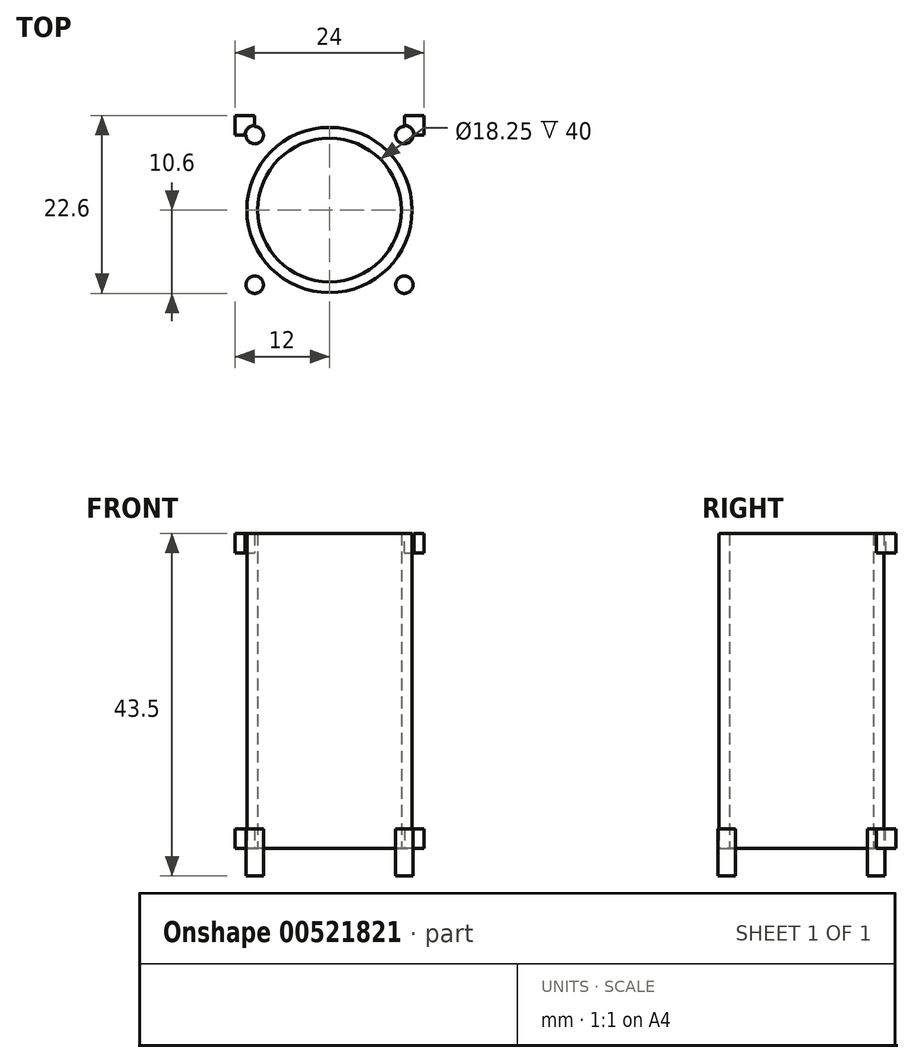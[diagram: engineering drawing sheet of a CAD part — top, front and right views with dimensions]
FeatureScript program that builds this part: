
annotation { "Feature Type Name" : "Feature", "Feature Type Description" : "" }
export const myFeature = defineFeature(function(context is Context, id is Id, definition is map)
    precondition{}
    {
        {
            var Q0;
            Q0=qCreatedBy(makeId("Top.planeOp"),FACE);
            var sketch = newSketch(context, id + "F0", { "sketchPlane" : qUnion([Q0])});
            skLineSegment(sketch, "E0.bottom", {"start": v(12, 12) * mm, "end": v(-12, 12) * mm});
            skLineSegment(sketch, "E0.top", {"start": v(12, -12) * mm, "end": v(-12, -12) * mm});
            skLineSegment(sketch, "E0.left", {"start": v(12, 12) * mm, "end": v(12, -12) * mm});
            skLineSegment(sketch, "E0.right", {"start": v(-12, 12) * mm, "end": v(-12, -12) * mm});
            skPoint(sketch, "E0.middle", {"position": v(0, 0) * mm});
            skLineSegment(sketch, "E1.bottom", {"start": v(-12, 12) * mm, "end": v(-9.5, 12) * mm});
            skLineSegment(sketch, "E1.top", {"start": v(-12, 9.5) * mm, "end": v(-9.5, 9.5) * mm});
            skLineSegment(sketch, "E1.left", {"start": v(-12, 12) * mm, "end": v(-12, 9.5) * mm});
            skLineSegment(sketch, "E1.right", {"start": v(-9.5, 12) * mm, "end": v(-9.5, 9.5) * mm});
            skLineSegment(sketch, "E2.bottom", {"start": v(12, 12) * mm, "end": v(9.5, 12) * mm});
            skLineSegment(sketch, "E2.top", {"start": v(12, 9.5) * mm, "end": v(9.5, 9.5) * mm});
            skLineSegment(sketch, "E2.left", {"start": v(12, 12) * mm, "end": v(12, 9.5) * mm});
            skLineSegment(sketch, "E2.right", {"start": v(9.5, 12) * mm, "end": v(9.5, 9.5) * mm});
            skLineSegment(sketch, "E3.bottom", {"start": v(12, -12) * mm, "end": v(9.5, -12) * mm});
            skLineSegment(sketch, "E3.top", {"start": v(12, -9.5) * mm, "end": v(9.5, -9.5) * mm});
            skLineSegment(sketch, "E3.left", {"start": v(12, -12) * mm, "end": v(12, -9.5) * mm});
            skLineSegment(sketch, "E3.right", {"start": v(9.5, -12) * mm, "end": v(9.5, -9.5) * mm});
            skLineSegment(sketch, "E4.bottom", {"start": v(-12, -12) * mm, "end": v(-9.5, -12) * mm});
            skLineSegment(sketch, "E4.top", {"start": v(-12, -9.5) * mm, "end": v(-9.5, -9.5) * mm});
            skLineSegment(sketch, "E4.left", {"start": v(-12, -12) * mm, "end": v(-12, -9.5) * mm});
            skLineSegment(sketch, "E4.right", {"start": v(-9.5, -12) * mm, "end": v(-9.5, -9.5) * mm});
            skCircle(sketch, "E5", {"center": v(0, 0) * mm, "radius": 9.12 * mm});
            skCircle(sketch, "E6", {"center": v(0, 0) * mm, "radius": 10.5 * mm});
            skCircle(sketch, "E7", {"center": v(9.5, 9.5) * mm, "radius": 1.1 * mm});
            skCircle(sketch, "E8", {"center": v(9.5, -9.5) * mm, "radius": 1.1 * mm});
            skCircle(sketch, "E9", {"center": v(-9.5, -9.5) * mm, "radius": 1.1 * mm});
            skCircle(sketch, "E10", {"center": v(-9.5, 9.5) * mm, "radius": 1.1 * mm});
            skSolve(sketch);
        }
        {
            var Q0;
            {var subQ8=sQuery(id+"F0.wireOp",EDGE,"E0.bottom");Q0=makeQuery(id+"F0.imprint","IMPRINT",FACE,{"disambiguationData":[TD([[makeQuery(id+"F0.imprint","IMPRINT",EDGE,{"derivedFrom":subQ8}),1.0]])]});}
            var Q1;
            Q1=makeQuery(id+"F0.imprint","IMPRINT",FACE,{"disambiguationData":[TD([[makeQuery(id+"F0.imprint","IMPRINT",EDGE,{"derivedFrom":sQuery(id+"F0.wireOp",EDGE,"E5")}),-1.0]])]});
            var Q2;
            {var subQ1=sQuery(id+"F0.wireOp",EDGE,"E3.bottom");Q2=makeQuery(id+"F0.imprint","IMPRINT",FACE,{"disambiguationData":[TD([[makeQuery(id+"F0.imprint","IMPRINT",EDGE,{"derivedFrom":subQ1}),-1.0]])]});}
            var Q3;
            {var subQ1=sQuery(id+"F0.wireOp",EDGE,"E4.bottom");Q3=makeQuery(id+"F0.imprint","IMPRINT",FACE,{"disambiguationData":[TD([[makeQuery(id+"F0.imprint","IMPRINT",EDGE,{"derivedFrom":subQ1}),1.0]])]});}
            var Q4;
            {var subQ1=sQuery(id+"F0.wireOp",EDGE,"E1.bottom");Q4=makeQuery(id+"F0.imprint","IMPRINT",FACE,{"disambiguationData":[TD([[makeQuery(id+"F0.imprint","IMPRINT",EDGE,{"derivedFrom":subQ1}),-1.0]])]});}
            var Q5;
            {var subQ1=sQuery(id+"F0.wireOp",EDGE,"E2.bottom");Q5=makeQuery(id+"F0.imprint","IMPRINT",FACE,{"disambiguationData":[TD([[makeQuery(id+"F0.imprint","IMPRINT",EDGE,{"derivedFrom":subQ1}),1.0]])]});}
            var Q6;
            {var subQ0=sQuery(id+"F0.wireOp",EDGE,"E2.right");var subQ1=sQuery(id+"F0.wireOp",EDGE,"E2.top");var subQ2=makeQuery(id+"F0.imprint","INTERSECT",VERTEX,{"derivedFrom":[subQ1,subQ0]});Q6=makeQuery(id+"F0.imprint","IMPRINT",FACE,{"disambiguationData":[TD([[makeQuery(id+"F0.imprint","IMPRINT",EDGE,{"disambiguationData":[TD([[subQ2,1.0]])],"derivedFrom":subQ1}),1.0]])]});}
            var Q7;
            {var subQ0=sQuery(id+"F0.wireOp",EDGE,"E2.right");var subQ1=sQuery(id+"F0.wireOp",EDGE,"E2.top");var subQ2=makeQuery(id+"F0.imprint","INTERSECT",VERTEX,{"derivedFrom":[subQ1,subQ0]});Q7=makeQuery(id+"F0.imprint","IMPRINT",FACE,{"disambiguationData":[TD([[makeQuery(id+"F0.imprint","IMPRINT",EDGE,{"disambiguationData":[TD([[subQ2,1.0]])],"derivedFrom":subQ1}),-1.0]])]});}
            var Q8;
            {var subQ0=sQuery(id+"F0.wireOp",EDGE,"E3.right");var subQ1=sQuery(id+"F0.wireOp",EDGE,"E3.top");var subQ2=makeQuery(id+"F0.imprint","INTERSECT",VERTEX,{"derivedFrom":[subQ1,subQ0]});Q8=makeQuery(id+"F0.imprint","IMPRINT",FACE,{"disambiguationData":[TD([[makeQuery(id+"F0.imprint","IMPRINT",EDGE,{"disambiguationData":[TD([[subQ2,1.0]])],"derivedFrom":subQ1}),-1.0]])]});}
            var Q9;
            {var subQ0=sQuery(id+"F0.wireOp",EDGE,"E3.right");var subQ1=sQuery(id+"F0.wireOp",EDGE,"E3.top");var subQ2=makeQuery(id+"F0.imprint","INTERSECT",VERTEX,{"derivedFrom":[subQ1,subQ0]});Q9=makeQuery(id+"F0.imprint","IMPRINT",FACE,{"disambiguationData":[TD([[makeQuery(id+"F0.imprint","IMPRINT",EDGE,{"disambiguationData":[TD([[subQ2,1.0]])],"derivedFrom":subQ1}),1.0]])]});}
            var Q10;
            {var subQ0=sQuery(id+"F0.wireOp",EDGE,"E4.right");var subQ1=sQuery(id+"F0.wireOp",EDGE,"E4.top");var subQ2=makeQuery(id+"F0.imprint","INTERSECT",VERTEX,{"derivedFrom":[subQ1,subQ0]});Q10=makeQuery(id+"F0.imprint","IMPRINT",FACE,{"disambiguationData":[TD([[makeQuery(id+"F0.imprint","IMPRINT",EDGE,{"disambiguationData":[TD([[subQ2,1.0]])],"derivedFrom":subQ1}),-1.0]])]});}
            var Q11;
            {var subQ0=sQuery(id+"F0.wireOp",EDGE,"E4.right");var subQ1=sQuery(id+"F0.wireOp",EDGE,"E4.top");var subQ2=makeQuery(id+"F0.imprint","INTERSECT",VERTEX,{"derivedFrom":[subQ1,subQ0]});Q11=makeQuery(id+"F0.imprint","IMPRINT",FACE,{"disambiguationData":[TD([[makeQuery(id+"F0.imprint","IMPRINT",EDGE,{"disambiguationData":[TD([[subQ2,1.0]])],"derivedFrom":subQ1}),1.0]])]});}
            var Q12;
            {var subQ0=sQuery(id+"F0.wireOp",EDGE,"E1.right");var subQ1=sQuery(id+"F0.wireOp",EDGE,"E1.top");var subQ2=makeQuery(id+"F0.imprint","INTERSECT",VERTEX,{"derivedFrom":[subQ1,subQ0]});Q12=makeQuery(id+"F0.imprint","IMPRINT",FACE,{"disambiguationData":[TD([[makeQuery(id+"F0.imprint","IMPRINT",EDGE,{"disambiguationData":[TD([[subQ2,1.0]])],"derivedFrom":subQ1}),-1.0]])]});}
            var Q13;
            {var subQ0=sQuery(id+"F0.wireOp",EDGE,"E1.right");var subQ1=sQuery(id+"F0.wireOp",EDGE,"E1.top");var subQ2=makeQuery(id+"F0.imprint","INTERSECT",VERTEX,{"derivedFrom":[subQ1,subQ0]});Q13=makeQuery(id+"F0.imprint","IMPRINT",FACE,{"disambiguationData":[TD([[makeQuery(id+"F0.imprint","IMPRINT",EDGE,{"disambiguationData":[TD([[subQ2,1.0]])],"derivedFrom":subQ1}),1.0]])]});}
            extrude(context, id + "F1", {"entities" : qUnion([Q0, Q1, Q2, Q3, Q4, Q5, Q6, Q7, Q8, Q9, Q10, Q11, Q12, Q13]), "depth" : 40 * mm, "offsetDistance" : 25 * mm});
        }
        {
            var Q0;
            Q0=qCreatedBy(makeId("Front.planeOp"),FACE);
            var sketch = newSketch(context, id + "F2", { "sketchPlane" : qUnion([Q0])});
            skLineSegment(sketch, "E11", {"start": v(0, 0) * mm, "end": v(17, 0) * mm});
            skLineSegment(sketch, "E12", {"start": v(17, 0) * mm, "end": v(17, 2.5) * mm});
            skLineSegment(sketch, "E13.bottom", {"start": v(17, 2.5) * mm, "end": v(11, 2.5) * mm});
            skLineSegment(sketch, "E13.top", {"start": v(17, 37.5) * mm, "end": v(11, 37.5) * mm});
            skLineSegment(sketch, "E13.left", {"start": v(17, 2.5) * mm, "end": v(17, 37.5) * mm});
            skLineSegment(sketch, "E13.right", {"start": v(11, 2.5) * mm, "end": v(11, 37.5) * mm});
            skLineSegment(sketch, "E14", {"start": v(0, 0) * mm, "end": v(0, 33.49) * mm});
            skSolve(sketch);
        }
        {
            var Q0;
            Q0=makeQuery(id+"F2.imprint","IMPRINT",FACE,{"disambiguationData":[TD([[makeQuery(id+"F2.imprint","IMPRINT",EDGE,{"derivedFrom":sQuery(id+"F2.wireOp",EDGE,"E13.bottom")}),-1.0]])]});
            var Q1;
            Q1=sQuery(id+"F2.wireOp",EDGE,"E14");
            revolve(context, id + "F3", {"operationType" : NewBodyOperationType.REMOVE, "entities" : qUnion([Q0]), "axis" : qUnion([Q1]), "revolveType" : RevolveType.FULL, "oppositeDirection" : true});
        }
        {
            var Q0;
            {var subQ0=sQuery(id+"F0.wireOp",EDGE,"E1.right");var subQ1=sQuery(id+"F0.wireOp",EDGE,"E1.top");var subQ2=makeQuery(id+"F0.imprint","INTERSECT",VERTEX,{"derivedFrom":[subQ1,subQ0]});Q0=makeQuery(id+"F0.imprint","IMPRINT",FACE,{"disambiguationData":[TD([[makeQuery(id+"F0.imprint","IMPRINT",EDGE,{"disambiguationData":[TD([[subQ2,1.0]])],"derivedFrom":subQ1}),1.0]])]});}
            var Q1;
            {var subQ0=sQuery(id+"F0.wireOp",EDGE,"E1.right");var subQ1=sQuery(id+"F0.wireOp",EDGE,"E1.top");var subQ2=makeQuery(id+"F0.imprint","INTERSECT",VERTEX,{"derivedFrom":[subQ1,subQ0]});Q1=makeQuery(id+"F0.imprint","IMPRINT",FACE,{"disambiguationData":[TD([[makeQuery(id+"F0.imprint","IMPRINT",EDGE,{"disambiguationData":[TD([[subQ2,1.0]])],"derivedFrom":subQ1}),-1.0]])]});}
            var Q2;
            {var subQ0=sQuery(id+"F0.wireOp",EDGE,"E4.right");var subQ1=sQuery(id+"F0.wireOp",EDGE,"E4.top");var subQ2=makeQuery(id+"F0.imprint","INTERSECT",VERTEX,{"derivedFrom":[subQ1,subQ0]});Q2=makeQuery(id+"F0.imprint","IMPRINT",FACE,{"disambiguationData":[TD([[makeQuery(id+"F0.imprint","IMPRINT",EDGE,{"disambiguationData":[TD([[subQ2,1.0]])],"derivedFrom":subQ1}),-1.0]])]});}
            var Q3;
            {var subQ0=sQuery(id+"F0.wireOp",EDGE,"E4.right");var subQ1=sQuery(id+"F0.wireOp",EDGE,"E4.top");var subQ2=makeQuery(id+"F0.imprint","INTERSECT",VERTEX,{"derivedFrom":[subQ1,subQ0]});Q3=makeQuery(id+"F0.imprint","IMPRINT",FACE,{"disambiguationData":[TD([[makeQuery(id+"F0.imprint","IMPRINT",EDGE,{"disambiguationData":[TD([[subQ2,1.0]])],"derivedFrom":subQ1}),1.0]])]});}
            var Q4;
            {var subQ0=sQuery(id+"F0.wireOp",EDGE,"E3.right");var subQ1=sQuery(id+"F0.wireOp",EDGE,"E3.top");var subQ2=makeQuery(id+"F0.imprint","INTERSECT",VERTEX,{"derivedFrom":[subQ1,subQ0]});Q4=makeQuery(id+"F0.imprint","IMPRINT",FACE,{"disambiguationData":[TD([[makeQuery(id+"F0.imprint","IMPRINT",EDGE,{"disambiguationData":[TD([[subQ2,1.0]])],"derivedFrom":subQ1}),-1.0]])]});}
            var Q5;
            {var subQ0=sQuery(id+"F0.wireOp",EDGE,"E3.right");var subQ1=sQuery(id+"F0.wireOp",EDGE,"E3.top");var subQ2=makeQuery(id+"F0.imprint","INTERSECT",VERTEX,{"derivedFrom":[subQ1,subQ0]});Q5=makeQuery(id+"F0.imprint","IMPRINT",FACE,{"disambiguationData":[TD([[makeQuery(id+"F0.imprint","IMPRINT",EDGE,{"disambiguationData":[TD([[subQ2,1.0]])],"derivedFrom":subQ1}),1.0]])]});}
            var Q6;
            {var subQ0=sQuery(id+"F0.wireOp",EDGE,"E2.right");var subQ1=sQuery(id+"F0.wireOp",EDGE,"E2.top");var subQ2=makeQuery(id+"F0.imprint","INTERSECT",VERTEX,{"derivedFrom":[subQ1,subQ0]});Q6=makeQuery(id+"F0.imprint","IMPRINT",FACE,{"disambiguationData":[TD([[makeQuery(id+"F0.imprint","IMPRINT",EDGE,{"disambiguationData":[TD([[subQ2,1.0]])],"derivedFrom":subQ1}),1.0]])]});}
            var Q7;
            {var subQ0=sQuery(id+"F0.wireOp",EDGE,"E2.right");var subQ1=sQuery(id+"F0.wireOp",EDGE,"E2.top");var subQ2=makeQuery(id+"F0.imprint","INTERSECT",VERTEX,{"derivedFrom":[subQ1,subQ0]});Q7=makeQuery(id+"F0.imprint","IMPRINT",FACE,{"disambiguationData":[TD([[makeQuery(id+"F0.imprint","IMPRINT",EDGE,{"disambiguationData":[TD([[subQ2,1.0]])],"derivedFrom":subQ1}),-1.0]])]});}
            extrude(context, id + "F4", {"entities" : qUnion([Q0, Q1, Q2, Q3, Q4, Q5, Q6, Q7]), "operationType" : NewBodyOperationType.ADD, "oppositeDirection" : true, "depth" : 3.5 * mm, "offsetDistance" : 25 * mm});
        }
        {
            var Q0;
            Q0=makeQuery(id+"F1.opExtrude","CAP_FACE",FACE,{"disambiguationData":[OSD([sQuery(id+"F0.wireOp",EDGE,"E0.bottom"),sQuery(id+"F0.wireOp",EDGE,"E0.top"),sQuery(id+"F0.wireOp",EDGE,"E0.left"),sQuery(id+"F0.wireOp",EDGE,"E0.right"),sQuery(id+"F0.wireOp",EDGE,"E1.bottom"),sQuery(id+"F0.wireOp",EDGE,"E1.left"),sQuery(id+"F0.wireOp",EDGE,"E2.bottom"),sQuery(id+"F0.wireOp",EDGE,"E2.left"),sQuery(id+"F0.wireOp",EDGE,"E3.bottom"),sQuery(id+"F0.wireOp",EDGE,"E3.left"),sQuery(id+"F0.wireOp",EDGE,"E4.bottom"),sQuery(id+"F0.wireOp",EDGE,"E4.left"),sQuery(id+"F0.wireOp",EDGE,"E5")])],"isStart":false});
            var sketch = newSketch(context, id + "F5", { "sketchPlane" : qUnion([Q0])});
            skLineSegment(sketch, "E15.bottom", {"start": v(12, 12) * mm, "end": v(-12, 12) * mm});
            skLineSegment(sketch, "E15.top", {"start": v(12, -12) * mm, "end": v(-12, -12) * mm});
            skLineSegment(sketch, "E15.left", {"start": v(12, 12) * mm, "end": v(12, -12) * mm});
            skLineSegment(sketch, "E15.right", {"start": v(-12, 12) * mm, "end": v(-12, -12) * mm});
            skPoint(sketch, "E15.middle", {"position": v(0, 0) * mm});
            skLineSegment(sketch, "E16.bottom", {"start": v(-12, 12) * mm, "end": v(-9.5, 12) * mm});
            skLineSegment(sketch, "E16.top", {"start": v(-12, 9.5) * mm, "end": v(-9.5, 9.5) * mm});
            skLineSegment(sketch, "E16.left", {"start": v(-12, 12) * mm, "end": v(-12, 9.5) * mm});
            skLineSegment(sketch, "E16.right", {"start": v(-9.5, 12) * mm, "end": v(-9.5, 9.5) * mm});
            skLineSegment(sketch, "E17.bottom", {"start": v(12, 12) * mm, "end": v(9.5, 12) * mm});
            skLineSegment(sketch, "E17.top", {"start": v(12, 9.5) * mm, "end": v(9.5, 9.5) * mm});
            skLineSegment(sketch, "E17.left", {"start": v(12, 12) * mm, "end": v(12, 9.5) * mm});
            skLineSegment(sketch, "E17.right", {"start": v(9.5, 12) * mm, "end": v(9.5, 9.5) * mm});
            skLineSegment(sketch, "E18.bottom", {"start": v(12, -12) * mm, "end": v(9.5, -12) * mm});
            skLineSegment(sketch, "E18.top", {"start": v(12, -9.5) * mm, "end": v(9.5, -9.5) * mm});
            skLineSegment(sketch, "E18.left", {"start": v(12, -12) * mm, "end": v(12, -9.5) * mm});
            skLineSegment(sketch, "E18.right", {"start": v(9.5, -12) * mm, "end": v(9.5, -9.5) * mm});
            skLineSegment(sketch, "E19.bottom", {"start": v(-12, -12) * mm, "end": v(-9.5, -12) * mm});
            skLineSegment(sketch, "E19.top", {"start": v(-12, -9.5) * mm, "end": v(-9.5, -9.5) * mm});
            skLineSegment(sketch, "E19.left", {"start": v(-12, -12) * mm, "end": v(-12, -9.5) * mm});
            skLineSegment(sketch, "E19.right", {"start": v(-9.5, -12) * mm, "end": v(-9.5, -9.5) * mm});
            skCircle(sketch, "E20", {"center": v(9.5, 9.5) * mm, "radius": 1.25 * mm});
            skCircle(sketch, "E21", {"center": v(9.5, -9.5) * mm, "radius": 1.25 * mm});
            skCircle(sketch, "E22", {"center": v(-9.5, -9.5) * mm, "radius": 1.25 * mm});
            skCircle(sketch, "E23", {"center": v(-9.5, 9.5) * mm, "radius": 1.25 * mm});
            skSolve(sketch);
        }
        {
            var Q0;
            {var subQ0=sQuery(id+"F5.wireOp",EDGE,"E18.right");var subQ1=sQuery(id+"F5.wireOp",EDGE,"E18.top");var subQ2=makeQuery(id+"F5.imprint","INTERSECT",VERTEX,{"derivedFrom":[subQ1,subQ0]});Q0=makeQuery(id+"F5.imprint","IMPRINT",FACE,{"disambiguationData":[TD([[makeQuery(id+"F5.imprint","IMPRINT",EDGE,{"disambiguationData":[TD([[subQ2,1.0]])],"derivedFrom":subQ1}),-1.0]])]});}
            var Q1;
            {var subQ0=sQuery(id+"F5.wireOp",EDGE,"E18.right");var subQ1=sQuery(id+"F5.wireOp",EDGE,"E18.top");var subQ2=makeQuery(id+"F5.imprint","INTERSECT",VERTEX,{"derivedFrom":[subQ1,subQ0]});Q1=makeQuery(id+"F5.imprint","IMPRINT",FACE,{"disambiguationData":[TD([[makeQuery(id+"F5.imprint","IMPRINT",EDGE,{"disambiguationData":[TD([[subQ2,1.0]])],"derivedFrom":subQ1}),1.0]])]});}
            var Q2;
            {var subQ0=sQuery(id+"F5.wireOp",EDGE,"E16.right");var subQ1=sQuery(id+"F5.wireOp",EDGE,"E16.top");var subQ2=makeQuery(id+"F5.imprint","INTERSECT",VERTEX,{"derivedFrom":[subQ1,subQ0]});Q2=makeQuery(id+"F5.imprint","IMPRINT",FACE,{"disambiguationData":[TD([[makeQuery(id+"F5.imprint","IMPRINT",EDGE,{"disambiguationData":[TD([[subQ2,1.0]])],"derivedFrom":subQ1}),1.0]])]});}
            var Q3;
            {var subQ0=sQuery(id+"F5.wireOp",EDGE,"E19.right");var subQ1=sQuery(id+"F5.wireOp",EDGE,"E19.top");var subQ2=makeQuery(id+"F5.imprint","INTERSECT",VERTEX,{"derivedFrom":[subQ1,subQ0]});Q3=makeQuery(id+"F5.imprint","IMPRINT",FACE,{"disambiguationData":[TD([[makeQuery(id+"F5.imprint","IMPRINT",EDGE,{"disambiguationData":[TD([[subQ2,1.0]])],"derivedFrom":subQ1}),1.0]])]});}
            var Q4;
            {var subQ0=sQuery(id+"F5.wireOp",EDGE,"E19.right");var subQ1=sQuery(id+"F5.wireOp",EDGE,"E19.top");var subQ2=makeQuery(id+"F5.imprint","INTERSECT",VERTEX,{"derivedFrom":[subQ1,subQ0]});Q4=makeQuery(id+"F5.imprint","IMPRINT",FACE,{"disambiguationData":[TD([[makeQuery(id+"F5.imprint","IMPRINT",EDGE,{"disambiguationData":[TD([[subQ2,1.0]])],"derivedFrom":subQ1}),-1.0]])]});}
            var Q5;
            {var subQ0=sQuery(id+"F5.wireOp",EDGE,"E16.right");var subQ1=sQuery(id+"F5.wireOp",EDGE,"E16.top");var subQ2=makeQuery(id+"F5.imprint","INTERSECT",VERTEX,{"derivedFrom":[subQ1,subQ0]});Q5=makeQuery(id+"F5.imprint","IMPRINT",FACE,{"disambiguationData":[TD([[makeQuery(id+"F5.imprint","IMPRINT",EDGE,{"disambiguationData":[TD([[subQ2,1.0]])],"derivedFrom":subQ1}),-1.0]])]});}
            var Q6;
            {var subQ0=sQuery(id+"F5.wireOp",EDGE,"E17.right");var subQ1=sQuery(id+"F5.wireOp",EDGE,"E17.top");var subQ2=makeQuery(id+"F5.imprint","INTERSECT",VERTEX,{"derivedFrom":[subQ1,subQ0]});Q6=makeQuery(id+"F5.imprint","IMPRINT",FACE,{"disambiguationData":[TD([[makeQuery(id+"F5.imprint","IMPRINT",EDGE,{"disambiguationData":[TD([[subQ2,1.0]])],"derivedFrom":subQ1}),1.0]])]});}
            var Q7;
            {var subQ0=sQuery(id+"F5.wireOp",EDGE,"E17.right");var subQ1=sQuery(id+"F5.wireOp",EDGE,"E17.top");var subQ2=makeQuery(id+"F5.imprint","INTERSECT",VERTEX,{"derivedFrom":[subQ1,subQ0]});Q7=makeQuery(id+"F5.imprint","IMPRINT",FACE,{"disambiguationData":[TD([[makeQuery(id+"F5.imprint","IMPRINT",EDGE,{"disambiguationData":[TD([[subQ2,1.0]])],"derivedFrom":subQ1}),-1.0]])]});}
            extrude(context, id + "F6", {"entities" : qUnion([Q0, Q1, Q2, Q3, Q4, Q5, Q6, Q7]), "operationType" : NewBodyOperationType.REMOVE, "oppositeDirection" : true, "depth" : 25 * mm, "offsetDistance" : 25 * mm});
        }
    });
